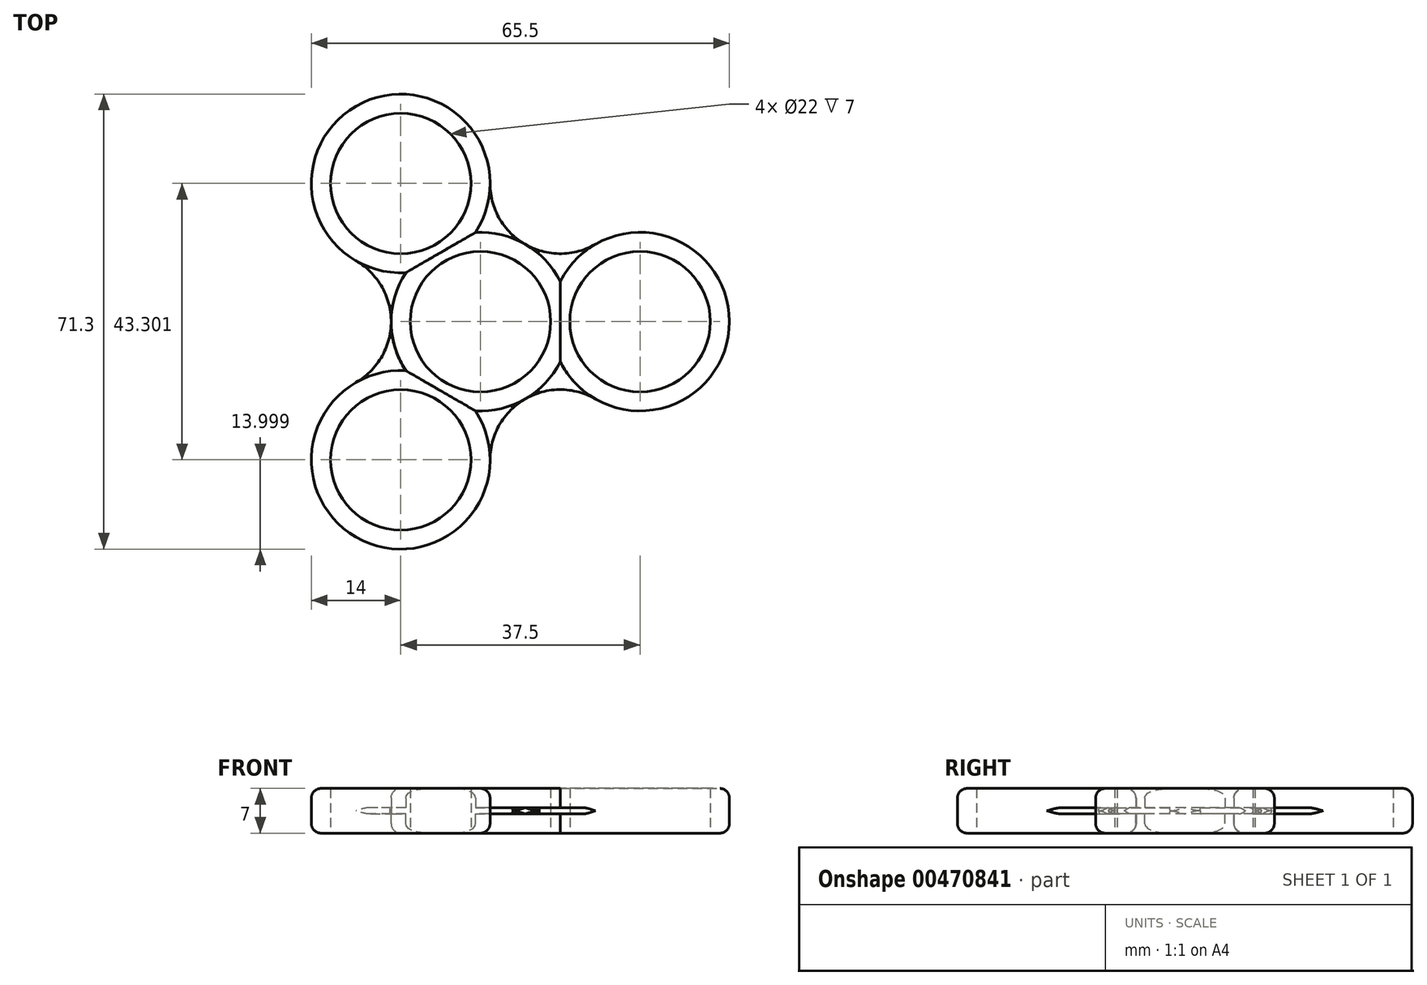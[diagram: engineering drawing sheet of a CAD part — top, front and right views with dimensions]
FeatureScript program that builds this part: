
annotation { "Feature Type Name" : "Feature", "Feature Type Description" : "" }
export const myFeature = defineFeature(function(context is Context, id is Id, definition is map)
    precondition{}
    {
        {
            var Q0;
            Q0=qCreatedBy(makeId("Top.planeOp"),FACE);
            var sketch = newSketch(context, id + "F0", { "sketchPlane" : qUnion([Q0])});
            skCircle(sketch, "E0", {"center": v(0, 0) * mm, "radius": 11 * mm});
            skArc(sketch, "E1", {"start": v(-11.71, 7.67) * mm, "mid": v(-14, 0) * mm, "end": v(-11.71, -7.67) * mm});
            skArc(sketch, "E2.cCircle", {"start": v(-11.71, 7.67) * mm, "mid": v(-14, 0) * mm, "end": v(-11.71, -7.67) * mm, "construction": true});
            skLineSegment(sketch, "E2.0", {"start": v(-14, -24.25) * mm, "end": v(-14, 24.25) * mm, "construction": true});
            skLineSegment(sketch, "E2.1", {"start": v(-14, 24.25) * mm, "end": v(28, 0) * mm, "construction": true});
            skLineSegment(sketch, "E2.2", {"start": v(28, 0) * mm, "end": v(-14, -24.25) * mm, "construction": true});
            skPoint(sketch, "E2.0.midPoint", {"position": v(-14, 0) * mm});
            skLineSegment(sketch, "E3", {"start": v(14, 0) * mm, "end": v(25, 0) * mm, "construction": true});
            skCircle(sketch, "E4", {"center": v(25, 0) * mm, "radius": 11 * mm});
            skArc(sketch, "E5", {"start": v(12.5, -6.3) * mm, "mid": v(39, 0) * mm, "end": v(12.5, 6.3) * mm});
            skLineSegment(sketch, "E6", {"start": v(-14, -24.25) * mm, "end": v(0, 0) * mm, "construction": true});
            skLineSegment(sketch, "E7", {"start": v(-7, -12.12) * mm, "end": v(-12.5, -21.65) * mm, "construction": true});
            skCircle(sketch, "E8", {"center": v(-12.5, -21.65) * mm, "radius": 11 * mm});
            skArc(sketch, "E9", {"start": v(-11.71, -7.67) * mm, "mid": v(-19.5, -33.77) * mm, "end": v(-0.79, -13.98) * mm});
            skLineSegment(sketch, "E10", {"start": v(0, 0) * mm, "end": v(-14, 24.25) * mm, "construction": true});
            skLineSegment(sketch, "E11", {"start": v(-7, 12.12) * mm, "end": v(-12.5, 21.65) * mm, "construction": true});
            skCircle(sketch, "E12", {"center": v(-12.5, 21.65) * mm, "radius": 11 * mm});
            skArc(sketch, "E13", {"start": v(-0.79, 13.98) * mm, "mid": v(-22.12, 31.83) * mm, "end": v(-5.5, 9.53) * mm});
            skLineSegment(sketch, "E14", {"start": v(-14, 0) * mm, "end": v(-25, 0) * mm, "construction": true});
            skArc(sketch, "E15", {"start": v(-19.5, -9.53) * mm, "mid": v(-14, 0) * mm, "end": v(-19.5, 9.53) * mm});
            skLineSegment(sketch, "E16", {"start": v(7, 12.12) * mm, "end": v(12.5, 21.65) * mm, "construction": true});
            skArc(sketch, "E17", {"start": v(1.5, 21.65) * mm, "mid": v(7, 12.12) * mm, "end": v(18, 12.12) * mm});
            skLineSegment(sketch, "E18", {"start": v(-25, 0) * mm, "end": v(12.5, 21.65) * mm, "construction": true});
            skCircle(sketch, "E19", {"center": v(-25, 0) * mm, "radius": 43.3 * mm, "construction": true});
            skCircle(sketch, "E20", {"center": v(12.5, 21.65) * mm, "radius": 43.3 * mm, "construction": true});
            skArc(sketch, "E21", {"start": v(18, -12.12) * mm, "mid": v(7, -12.12) * mm, "end": v(1.5, -21.65) * mm});
            skArc(sketch, "E22.trimOffspring", {"start": v(14, 0) * mm, "mid": v(9.62, 10.17) * mm, "end": v(-0.79, 13.98) * mm, "construction": true});
            skArc(sketch, "E23.trimOffspring", {"start": v(14, 0) * mm, "mid": v(9.62, 10.17) * mm, "end": v(-0.79, 13.98) * mm});
            skArc(sketch, "E24.trimOffspring", {"start": v(-0.79, -13.98) * mm, "mid": v(7, -12.12) * mm, "end": v(12.5, -6.3) * mm, "construction": true});
            skArc(sketch, "E25.trimOffspring", {"start": v(-0.79, -13.98) * mm, "mid": v(7, -12.12) * mm, "end": v(12.5, -6.3) * mm});
            skSolve(sketch);
        }
        {
            var Q0;
            Q0=makeQuery(id+"F0.imprint","IMPRINT",FACE,{"disambiguationData":[TD([[makeQuery(id+"F0.imprint","IMPRINT",EDGE,{"derivedFrom":sQuery(id+"F0.wireOp",EDGE,"E0")}),-1.0]])]});
            extrude(context, id + "F1", {"entities" : qUnion([Q0]), "depth" : 3.5 * mm, "offsetDistance" : 25 * mm});
        }
        {
            var Q0;
            {var subQ0=sQuery(id+"F0.wireOp",EDGE,"E13");var subQ1=sQuery(id+"F0.wireOp",EDGE,"E1");var subQ2=makeQuery(id+"F0.imprint","INTERSECT",VERTEX,{"derivedFrom":[subQ1,subQ0]});Q0=makeQuery(id+"F0.imprint","IMPRINT",FACE,{"disambiguationData":[TD([[makeQuery(id+"F0.imprint","IMPRINT",EDGE,{"disambiguationData":[TD([[subQ2,-1.0]])],"derivedFrom":subQ1}),-1.0]])]});}
            var Q1;
            {var subQ0=sQuery(id+"F0.wireOp",EDGE,"E9");var subQ1=sQuery(id+"F0.wireOp",EDGE,"E1");var subQ2=makeQuery(id+"F0.imprint","INTERSECT",VERTEX,{"derivedFrom":[subQ1,subQ0]});Q1=makeQuery(id+"F0.imprint","IMPRINT",FACE,{"disambiguationData":[TD([[makeQuery(id+"F0.imprint","IMPRINT",EDGE,{"disambiguationData":[TD([[subQ2,1.0]])],"derivedFrom":subQ1}),-1.0]])]});}
            var Q2;
            {var subQ0=sQuery(id+"F0.wireOp",EDGE,"E23.trimOffspring");var subQ1=sQuery(id+"F0.wireOp",EDGE,"E13");var subQ2=makeQuery(id+"F0.imprint","INTERSECT",VERTEX,{"derivedFrom":[subQ1,subQ0]});Q2=makeQuery(id+"F0.imprint","IMPRINT",FACE,{"disambiguationData":[TD([[makeQuery(id+"F0.imprint","IMPRINT",EDGE,{"disambiguationData":[TD([[subQ2,-1.0]])],"derivedFrom":subQ1}),-1.0]])]});}
            var Q3;
            {var subQ0=sQuery(id+"F0.wireOp",EDGE,"E23.trimOffspring");var subQ1=sQuery(id+"F0.wireOp",EDGE,"E5");var subQ2=makeQuery(id+"F0.imprint","INTERSECT",VERTEX,{"derivedFrom":[subQ1,subQ0]});Q3=makeQuery(id+"F0.imprint","IMPRINT",FACE,{"disambiguationData":[TD([[makeQuery(id+"F0.imprint","IMPRINT",EDGE,{"disambiguationData":[TD([[subQ2,1.0]])],"derivedFrom":subQ1}),-1.0]])]});}
            var Q4;
            {var subQ0=sQuery(id+"F0.wireOp",EDGE,"E25.trimOffspring");var subQ1=sQuery(id+"F0.wireOp",EDGE,"E5");var subQ2=makeQuery(id+"F0.imprint","INTERSECT",VERTEX,{"derivedFrom":[subQ1,subQ0]});Q4=makeQuery(id+"F0.imprint","IMPRINT",FACE,{"disambiguationData":[TD([[makeQuery(id+"F0.imprint","IMPRINT",EDGE,{"disambiguationData":[TD([[subQ2,-1.0]])],"derivedFrom":subQ1}),-1.0]])]});}
            var Q5;
            {var subQ0=sQuery(id+"F0.wireOp",EDGE,"E25.trimOffspring");var subQ1=sQuery(id+"F0.wireOp",EDGE,"E9");var subQ2=makeQuery(id+"F0.imprint","INTERSECT",VERTEX,{"derivedFrom":[subQ1,subQ0]});Q5=makeQuery(id+"F0.imprint","IMPRINT",FACE,{"disambiguationData":[TD([[makeQuery(id+"F0.imprint","IMPRINT",EDGE,{"disambiguationData":[TD([[subQ2,1.0]])],"derivedFrom":subQ1}),-1.0]])]});}
            extrude(context, id + "F2", {"entities" : qUnion([Q0, Q1, Q2, Q3, Q4, Q5]), "operationType" : NewBodyOperationType.ADD, "depth" : 0.5 * mm, "offsetDistance" : 25 * mm});
        }
        {
            var Q0;
            Q0=makeQuery(id+"F1.opExtrude","SWEPT_BODY",BODY,{"disambiguationData":[OSD([sQuery(id+"F0.wireOp",EDGE,"E0"),sQuery(id+"F0.wireOp",EDGE,"E1"),sQuery(id+"F0.wireOp",EDGE,"E4"),sQuery(id+"F0.wireOp",EDGE,"E5"),sQuery(id+"F0.wireOp",EDGE,"E8"),sQuery(id+"F0.wireOp",EDGE,"E9"),sQuery(id+"F0.wireOp",EDGE,"E12"),sQuery(id+"F0.wireOp",EDGE,"E13"),sQuery(id+"F0.wireOp",EDGE,"E23.trimOffspring"),sQuery(id+"F0.wireOp",EDGE,"E25.trimOffspring")])]});
            var Q1;
            {var subQ0=sQuery(id+"F0.wireOp",EDGE,"E23.trimOffspring");var subQ1=sQuery(id+"F0.wireOp",EDGE,"E17");var subQ2=sQuery(id+"F0.wireOp",EDGE,"E13");var subQ3=sQuery(id+"F0.wireOp",EDGE,"E25.trimOffspring");var subQ4=sQuery(id+"F0.wireOp",EDGE,"E21");var subQ5=sQuery(id+"F0.wireOp",EDGE,"E9");var subQ6=sQuery(id+"F0.wireOp",EDGE,"E5");var subQ7=sQuery(id+"F0.wireOp",EDGE,"E15");var subQ8=sQuery(id+"F0.wireOp",EDGE,"E1");Q1=makeQuery(id+"F2.boolean.opBoolean","MERGE",FACE,{"derivedFrom":[makeQuery(id+"F1.opExtrude","CAP_FACE",FACE,{"disambiguationData":[OSD([sQuery(id+"F0.wireOp",EDGE,"E0"),subQ8,sQuery(id+"F0.wireOp",EDGE,"E4"),subQ6,sQuery(id+"F0.wireOp",EDGE,"E8"),subQ5,sQuery(id+"F0.wireOp",EDGE,"E12"),subQ2,subQ0,subQ3])],"isStart":true}),makeQuery(id+"F2.opExtrude","CAP_FACE",FACE,{"disambiguationData":[OSD([subQ8,subQ2,subQ7])],"isStart":true}),makeQuery(id+"F2.opExtrude","CAP_FACE",FACE,{"disambiguationData":[OSD([subQ8,subQ5,subQ7])],"isStart":true}),makeQuery(id+"F2.opExtrude","CAP_FACE",FACE,{"disambiguationData":[OSD([subQ6,subQ4,subQ3])],"isStart":true}),makeQuery(id+"F2.opExtrude","CAP_FACE",FACE,{"disambiguationData":[OSD([subQ6,subQ1,subQ0])],"isStart":true}),makeQuery(id+"F2.opExtrude","CAP_FACE",FACE,{"disambiguationData":[OSD([subQ5,subQ4,subQ3])],"isStart":true}),makeQuery(id+"F2.opExtrude","CAP_FACE",FACE,{"disambiguationData":[OSD([subQ2,subQ1,subQ0])],"isStart":true})]});}
            mirror(context, id + "F3", {"operationType" : NewBodyOperationType.ADD, "entities" : qUnion([Q0]), "mirrorPlane" : qUnion([Q1])});
        }
        {
            var Q0;
            Q0=makeQuery(id+"F1.opExtrude","CAP_EDGE",EDGE,{"disambiguationData":[OSD([sQuery(id+"F0.wireOp",EDGE,"E13")])],"isStart":false});
            var Q1;
            Q1=makeQuery(id+"F1.opExtrude","CAP_EDGE",EDGE,{"disambiguationData":[OSD([sQuery(id+"F0.wireOp",EDGE,"E1")])],"isStart":false});
            var Q2;
            Q2=makeQuery(id+"F1.opExtrude","CAP_EDGE",EDGE,{"disambiguationData":[OSD([sQuery(id+"F0.wireOp",EDGE,"E9")])],"isStart":false});
            var Q3;
            Q3=makeQuery(id+"F1.opExtrude","CAP_EDGE",EDGE,{"disambiguationData":[OSD([sQuery(id+"F0.wireOp",EDGE,"E25.trimOffspring")])],"isStart":false});
            var Q4;
            Q4=makeQuery(id+"F1.opExtrude","CAP_EDGE",EDGE,{"disambiguationData":[OSD([sQuery(id+"F0.wireOp",EDGE,"E23.trimOffspring")])],"isStart":false});
            var Q5;
            Q5=makeQuery(id+"F1.opExtrude","CAP_EDGE",EDGE,{"disambiguationData":[OSD([sQuery(id+"F0.wireOp",EDGE,"E5")])],"isStart":false});
            var Q6;
            Q6=makeQuery(id+"F3.opPattern","COPY",EDGE,{"derivedFrom":makeQuery(id+"F1.opExtrude","CAP_EDGE",EDGE,{"disambiguationData":[OSD([sQuery(id+"F0.wireOp",EDGE,"E5")])],"isStart":false}),"instanceName":"1"});
            var Q7;
            Q7=makeQuery(id+"F3.opPattern","COPY",EDGE,{"derivedFrom":makeQuery(id+"F1.opExtrude","CAP_EDGE",EDGE,{"disambiguationData":[OSD([sQuery(id+"F0.wireOp",EDGE,"E25.trimOffspring")])],"isStart":false}),"instanceName":"1"});
            var Q8;
            Q8=makeQuery(id+"F3.opPattern","COPY",EDGE,{"derivedFrom":makeQuery(id+"F1.opExtrude","CAP_EDGE",EDGE,{"disambiguationData":[OSD([sQuery(id+"F0.wireOp",EDGE,"E23.trimOffspring")])],"isStart":false}),"instanceName":"1"});
            var Q9;
            Q9=makeQuery(id+"F3.opPattern","COPY",EDGE,{"derivedFrom":makeQuery(id+"F1.opExtrude","CAP_EDGE",EDGE,{"disambiguationData":[OSD([sQuery(id+"F0.wireOp",EDGE,"E13")])],"isStart":false}),"instanceName":"1"});
            var Q10;
            Q10=makeQuery(id+"F3.opPattern","COPY",EDGE,{"derivedFrom":makeQuery(id+"F1.opExtrude","CAP_EDGE",EDGE,{"disambiguationData":[OSD([sQuery(id+"F0.wireOp",EDGE,"E1")])],"isStart":false}),"instanceName":"1"});
            var Q11;
            Q11=makeQuery(id+"F3.opPattern","COPY",EDGE,{"derivedFrom":makeQuery(id+"F1.opExtrude","CAP_EDGE",EDGE,{"disambiguationData":[OSD([sQuery(id+"F0.wireOp",EDGE,"E9")])],"isStart":false}),"instanceName":"1"});
            fillet(context, id + "F4", {"entities" : qUnion([Q0, Q1, Q2, Q3, Q4, Q5, Q6, Q7, Q8, Q9, Q10, Q11]), "radius" : 1.5 * mm, "allowEdgeOverflow" : false});
        }
        {
            var Q0;
            {var subQ0=sQuery(id+"F0.wireOp",EDGE,"E17");Q0=makeQuery(id+"F2.opExtrude","CAP_EDGE",EDGE,{"disambiguationData":[OSD([subQ0]),TDD([makeQuery(id+"F0.imprint","IMPRINT",EDGE,{"disambiguationData":[TD([[makeQuery(id+"F0.imprint","INTERSECT",VERTEX,{"derivedFrom":[sQuery(id+"F0.wireOp",EDGE,"E5"),subQ0]}),1.0]])],"derivedFrom":subQ0})])],"isStart":false});}
            var Q1;
            {var subQ0=sQuery(id+"F0.wireOp",EDGE,"E17");Q1=makeQuery(id+"F2.opExtrude","CAP_EDGE",EDGE,{"disambiguationData":[OSD([subQ0]),TDD([makeQuery(id+"F0.imprint","IMPRINT",EDGE,{"disambiguationData":[TD([[makeQuery(id+"F0.imprint","INTERSECT",VERTEX,{"derivedFrom":[sQuery(id+"F0.wireOp",EDGE,"E13"),subQ0]}),-1.0]])],"derivedFrom":subQ0})])],"isStart":false});}
            var Q2;
            {var subQ0=sQuery(id+"F0.wireOp",EDGE,"E17");Q2=makeQuery(id+"F3.opPattern","COPY",EDGE,{"derivedFrom":makeQuery(id+"F2.opExtrude","CAP_EDGE",EDGE,{"disambiguationData":[OSD([subQ0]),TDD([makeQuery(id+"F0.imprint","IMPRINT",EDGE,{"disambiguationData":[TD([[makeQuery(id+"F0.imprint","INTERSECT",VERTEX,{"derivedFrom":[sQuery(id+"F0.wireOp",EDGE,"E5"),subQ0]}),1.0]])],"derivedFrom":subQ0})])],"isStart":false}),"instanceName":"1"});}
            var Q3;
            {var subQ0=sQuery(id+"F0.wireOp",EDGE,"E17");Q3=makeQuery(id+"F3.opPattern","COPY",EDGE,{"derivedFrom":makeQuery(id+"F2.opExtrude","CAP_EDGE",EDGE,{"disambiguationData":[OSD([subQ0]),TDD([makeQuery(id+"F0.imprint","IMPRINT",EDGE,{"disambiguationData":[TD([[makeQuery(id+"F0.imprint","INTERSECT",VERTEX,{"derivedFrom":[sQuery(id+"F0.wireOp",EDGE,"E13"),subQ0]}),-1.0]])],"derivedFrom":subQ0})])],"isStart":false}),"instanceName":"1"});}
            var Q4;
            {var subQ0=sQuery(id+"F0.wireOp",EDGE,"E15");Q4=makeQuery(id+"F2.opExtrude","CAP_EDGE",EDGE,{"disambiguationData":[OSD([subQ0]),TDD([makeQuery(id+"F0.imprint","IMPRINT",EDGE,{"disambiguationData":[TD([[makeQuery(id+"F0.imprint","INTERSECT",VERTEX,{"derivedFrom":[sQuery(id+"F0.wireOp",EDGE,"E13"),subQ0]}),1.0]])],"derivedFrom":subQ0})])],"isStart":false});}
            var Q5;
            {var subQ0=sQuery(id+"F0.wireOp",EDGE,"E15");var subQ2=makeQuery(id+"F2.boolean.opBoolean","MERGE",FACE,{"derivedFrom":[makeQuery(id+"F2.opExtrude","SWEPT_FACE",FACE,{"disambiguationData":[OSD([subQ0]),TDD([makeQuery(id+"F0.imprint","IMPRINT",EDGE,{"disambiguationData":[TD([[makeQuery(id+"F0.imprint","INTERSECT",VERTEX,{"derivedFrom":[sQuery(id+"F0.wireOp",EDGE,"E9"),subQ0]}),-1.0]])],"derivedFrom":subQ0})])]}),makeQuery(id+"F2.opExtrude","SWEPT_FACE",FACE,{"disambiguationData":[OSD([subQ0]),TDD([makeQuery(id+"F0.imprint","IMPRINT",EDGE,{"disambiguationData":[TD([[makeQuery(id+"F0.imprint","INTERSECT",VERTEX,{"derivedFrom":[sQuery(id+"F0.wireOp",EDGE,"E13"),subQ0]}),1.0]])],"derivedFrom":subQ0})])]})]});Q5=makeQuery(id+"F3.boolean.opBoolean","MERGE",FACE,{"derivedFrom":[subQ2,makeQuery(id+"F3.opPattern","COPY",FACE,{"derivedFrom":subQ2,"instanceName":"1"})]});}
            var Q6;
            {var subQ0=sQuery(id+"F0.wireOp",EDGE,"E15");Q6=makeQuery(id+"F2.opExtrude","CAP_EDGE",EDGE,{"disambiguationData":[OSD([subQ0]),TDD([makeQuery(id+"F0.imprint","IMPRINT",EDGE,{"disambiguationData":[TD([[makeQuery(id+"F0.imprint","INTERSECT",VERTEX,{"derivedFrom":[sQuery(id+"F0.wireOp",EDGE,"E9"),subQ0]}),-1.0]])],"derivedFrom":subQ0})])],"isStart":false});}
            var Q7;
            {var subQ0=sQuery(id+"F0.wireOp",EDGE,"E21");var subQ2=makeQuery(id+"F2.boolean.opBoolean","MERGE",FACE,{"derivedFrom":[makeQuery(id+"F2.opExtrude","SWEPT_FACE",FACE,{"disambiguationData":[OSD([subQ0]),TDD([makeQuery(id+"F0.imprint","IMPRINT",EDGE,{"disambiguationData":[TD([[makeQuery(id+"F0.imprint","INTERSECT",VERTEX,{"derivedFrom":[sQuery(id+"F0.wireOp",EDGE,"E5"),subQ0]}),-1.0]])],"derivedFrom":subQ0})])]}),makeQuery(id+"F2.opExtrude","SWEPT_FACE",FACE,{"disambiguationData":[OSD([subQ0]),TDD([makeQuery(id+"F0.imprint","IMPRINT",EDGE,{"disambiguationData":[TD([[makeQuery(id+"F0.imprint","INTERSECT",VERTEX,{"derivedFrom":[sQuery(id+"F0.wireOp",EDGE,"E9"),subQ0]}),1.0]])],"derivedFrom":subQ0})])]})]});Q7=makeQuery(id+"F3.boolean.opBoolean","MERGE",FACE,{"derivedFrom":[subQ2,makeQuery(id+"F3.opPattern","COPY",FACE,{"derivedFrom":subQ2,"instanceName":"1"})]});}
            fillet(context, id + "F5", {"entities" : qUnion([Q0, Q1, Q2, Q3, Q4, Q5, Q6, Q7]), "radius" : 0.5 * mm, "tangentPropagation" : true, "allowEdgeOverflow" : false});
        }
    });
